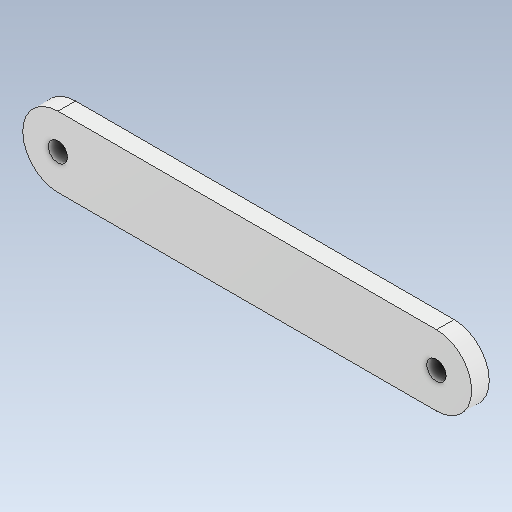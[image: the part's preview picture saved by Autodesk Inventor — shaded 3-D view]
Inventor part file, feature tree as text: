
AUTODESK INVENTOR PART (.ipt)
format: ipt  version: 2021 (Build 250183000, 183)  size: 103,424 bytes
history: native  units: in
note: dims shown in document units (in); Inventor stores cm internally (conversion verified against a paired STEP export)
features: extrude x1, sketch x1
ambient origin geometry x8: Origin, YZ Plane, XZ Plane, XY Plane, X Axis, Y Axis, Z Axis, Center Point
bodies: Solid1 (feature_tree)
feature tree (2):
  extrude  "Extrusion1"  Depth=1.5748in
  sketch  "Sketch1"  dims[d0=8.4646in d1=1.5748in d4=0.4331in d5=0.4331in d6=0.3937in d7=0.0in]
